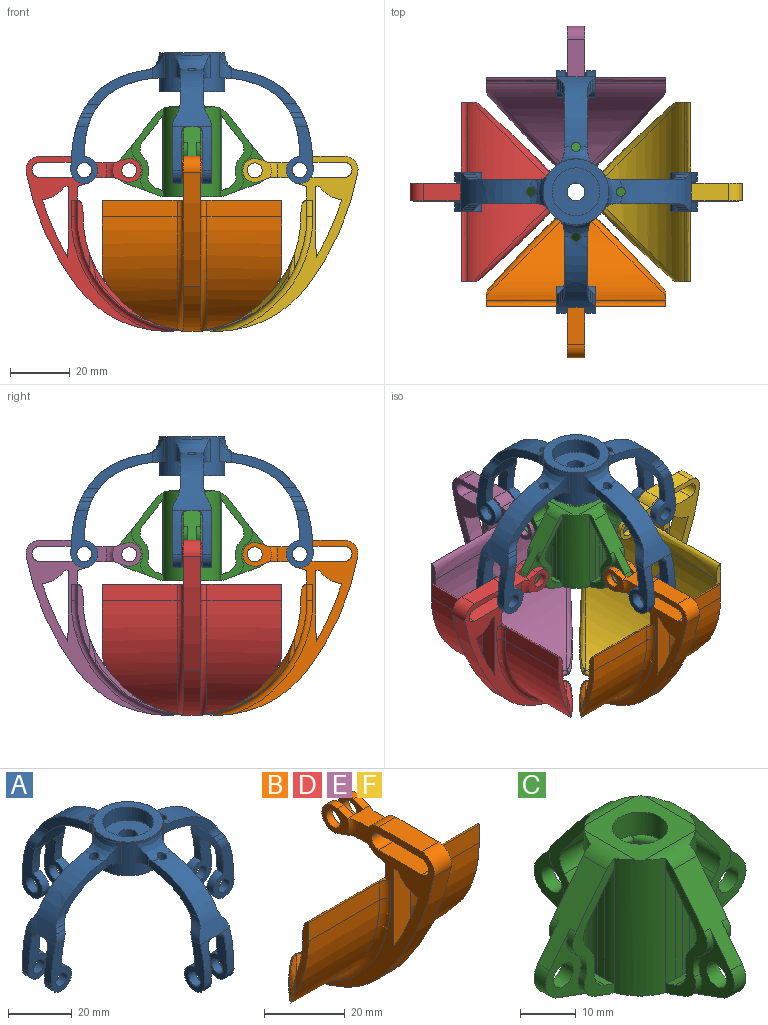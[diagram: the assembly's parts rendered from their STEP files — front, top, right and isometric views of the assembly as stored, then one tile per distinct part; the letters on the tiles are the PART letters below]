
ASSEMBLY  parts=6 mates=3
PART A: 124 faces, bbox 81x81x43.8 mm
  f0: extruded ~23.73x18.99mm, area 274.3mm2, adj f2,f27,f36,f37,f41,f42,f43,f44
  f1: extruded ~25.65x16.4mm, area 266.5mm2, adj f25,f33,f36,f37,f39,f42,f43,f44
  f2: bspline ~20.2x7.03mm, area 69.4mm2, adj f0,f33,f36,f37,f55,f56,f123
  f3: extruded ~23.73x18.99mm, area 274.3mm2, adj f5,f23,f57,f58,f62,f63,f64,f65
  f4: extruded ~25.65x16.4mm, area 266.5mm2, adj f21,f33,f57,f58,f60,f63,f64,f65
  f5: bspline ~20.2x7.03mm, area 63.5mm2, adj f3,f33,f57,f58,f76,f77,f122
  f6: extruded ~23.73x18.99mm, area 274.3mm2, adj f8,f19,f78,f79,f83,f84,f85,f86
  f7: extruded ~25.65x16.4mm, area 266.6mm2, adj f17,f33,f78,f79,f81,f84,f85,f86
  f8: bspline ~20.2x7.03mm, area 67.5mm2, adj f6,f33,f78,f79,f97,f98,f121
  f9: extruded ~23.73x18.99mm, area 274.3mm2, adj f11,f15,f99,f100,f104,f105,f106,f107
  f10: extruded ~25.65x16.4mm, area 266.5mm2, adj f13,f33,f99,f100,f102,f105,f106,f107
  f11: bspline ~20.2x7.03mm, area 63.5mm2, adj f9,f33,f99,f100,f118,f119,f120
  f12: cylinder r=4.5mm len=9mm, axis (-1,0,0), area 63.6mm2, adj f13,f15,f106,f114
  f13: extruded ~10x5mm, area 32.4mm2, adj f10,f12,f106,f114,f117
  f14: cylinder r=2.5mm len=5mm, axis (-1,0,0), area 47.1mm2, adj f106,f114
  f15: extruded ~14.5x5mm, area 46.1mm2, adj f9,f12,f106,f114,f117
  f16: cylinder r=4.5mm len=9mm, axis (0,-1,0), area 63.6mm2, adj f17,f19,f85,f93
  f17: extruded ~10x5mm, area 32.4mm2, adj f7,f16,f85,f93,f96
  f18: cylinder r=2.5mm len=5mm, axis (0,-1,0), area 47.1mm2, adj f85,f93
  f19: extruded ~14.5x5mm, area 46.1mm2, adj f6,f16,f85,f93,f96
  f20: cylinder r=4.5mm len=9mm, axis (1,0,0), area 63.6mm2, adj f21,f23,f64,f72
  f21: extruded ~10x5mm, area 32.4mm2, adj f4,f20,f64,f72,f75
  f22: cylinder r=2.5mm len=5mm, axis (1,0,0), area 47.1mm2, adj f64,f72
  f23: extruded ~14.5x5mm, area 46.1mm2, adj f3,f20,f64,f72,f75
  f24: cylinder r=4.5mm len=9mm, axis (0,1,0), area 63.6mm2, adj f25,f27,f43,f51
  f25: extruded ~10x5mm, area 32.4mm2, adj f1,f24,f43,f51,f54
  f26: cylinder r=2.5mm len=5mm, axis (0,1,0), area 47.1mm2, adj f43,f51
  f27: extruded ~14.5x5mm, area 46.1mm2, adj f0,f24,f43,f51,f54
  f28: cylinder r=3mm len=6mm, axis (0,0,-1), area 56.5mm2, adj f29,f30
  f29: plane 16x16mm, normal (0,0,1), area 172.8mm2, adj f28,f32
  f30: plane 16x16mm, normal (0,0,-1), area 172.8mm2, adj f28,f31
  f31: cylinder r=8mm len=16mm, axis (0,0,-1), area 251.3mm2, adj f30,f35
  f32: cylinder r=8mm len=16mm, axis (0,0,-1), area 251.3mm2, adj f29,f34
  f33: cylinder r=11mm len=22mm, axis (0,0,-1), area 490.5mm2, adj f1,f2,f4,f5,f7,f8,f10,f11
  f34: plane 22x22mm, normal (0,0,1), area 179.1mm2, adj f32,f33
  f35: plane 22x22mm, normal (0,0,-1), area 179.1mm2, adj f31,f33
  f36: plane 23.74x12.98mm, normal (0,-1,0), area 71mm2, adj f0,f1,f2,f49,f56
  f37: plane 23.68x12.9mm, normal (0,1,0), area 70.7mm2, adj f0,f1,f2,f47,f55
  f38: cylinder r=4.5mm len=9mm, axis (0,1,0), area 63.6mm2, adj f39,f41,f42,f52
  f39: extruded ~10x5mm, area 32.4mm2, adj f1,f38,f42,f52,f53
  f40: cylinder r=2.5mm len=5mm, axis (0,1,0), area 47.1mm2, adj f42,f52
  f41: extruded ~14.5x5mm, area 46.1mm2, adj f0,f38,f42,f52,f53
  f42: plane 19.26x9mm, normal (0,-1,0), area 88.8mm2, adj f0,f1,f38,f39,f40,f41,f48
  f43: plane 19.26x9mm, normal (0,1,0), area 89mm2, adj f0,f1,f24,f25,f26,f27,f46
  f44: plane 4.47x1.4mm, normal (0,-0.86,0.51), area 6.1mm2, adj f0,f1,f48,f49
  f45: plane 4.53x1.5mm, normal (0,0.86,0.5), area 6.6mm2, adj f0,f1,f46,f47
  f46: cylinder r=6mm len=4.91mm, axis (1,0,0), area 12.1mm2, adj f0,f1,f43,f45
  f47: cylinder r=6mm len=5.78mm, axis (1,0,0), area 12.5mm2, adj f0,f1,f37,f45
  f48: cylinder r=6mm len=4.92mm, axis (-1,0,0), area 12.3mm2, adj f0,f1,f42,f44
  f49: cylinder r=6mm len=5.77mm, axis (-1,0,0), area 12.6mm2, adj f0,f1,f36,f44
  f50: plane 3.83x3mm, normal (0,0,-1), area 11.5mm2, adj f0,f1,f53,f54
  f51: plane 17.19x9mm, normal (0,-1,0), area 80.9mm2, adj f24,f25,f26,f27,f54
  f52: plane 17.19x9mm, normal (0,1,0), area 80.9mm2, adj f38,f39,f40,f41,f53
  f53: cylinder r=2mm len=4.38mm, axis (1,0,0), area 12.1mm2, adj f39,f41,f50,f52
  f54: cylinder r=2mm len=4.38mm, axis (-1,0,0), area 12.1mm2, adj f25,f27,f50,f51
  f55: cylinder r=5mm len=8.04mm, axis (0,0,-1), area 27mm2, adj f1,f2,f33,f37
  f56: cylinder r=5mm len=8.04mm, axis (0,0,-1), area 27mm2, adj f1,f2,f33,f36
  f57: plane 23.74x12.98mm, normal (-1,0,0), area 71mm2, adj f3,f4,f5,f70,f77
  f58: plane 23.68x12.9mm, normal (1,0,0), area 70.7mm2, adj f3,f4,f5,f68,f76
  f59: cylinder r=4.5mm len=9mm, axis (1,0,0), area 63.6mm2, adj f60,f62,f63,f73
  f60: extruded ~10x5mm, area 32.4mm2, adj f4,f59,f63,f73,f74
  f61: cylinder r=2.5mm len=5mm, axis (1,0,0), area 47.1mm2, adj f63,f73
  f62: extruded ~14.5x5mm, area 46.1mm2, adj f3,f59,f63,f73,f74
  f63: plane 19.26x9mm, normal (-1,0,0), area 88.8mm2, adj f3,f4,f59,f60,f61,f62,f69
  f64: plane 19.26x9mm, normal (1,0,0), area 89mm2, adj f3,f4,f20,f21,f22,f23,f67
  f65: plane 4.47x1.4mm, normal (-0.86,0,0.51), area 6.1mm2, adj f3,f4,f69,f70
  f66: plane 4.53x1.5mm, normal (0.86,0,0.5), area 6.6mm2, adj f3,f4,f67,f68
  f67: cylinder r=6mm len=4.91mm, axis (0,-1,0), area 12.1mm2, adj f3,f4,f64,f66
  f68: cylinder r=6mm len=5.78mm, axis (0,-1,0), area 12.5mm2, adj f3,f4,f58,f66
  f69: cylinder r=6mm len=4.92mm, axis (0,1,0), area 12.3mm2, adj f3,f4,f63,f65
  f70: cylinder r=6mm len=5.77mm, axis (0,1,0), area 12.6mm2, adj f3,f4,f57,f65
  f71: plane 3.83x3mm, normal (0,0,-1), area 11.5mm2, adj f3,f4,f74,f75
  f72: plane 17.19x9mm, normal (-1,0,0), area 80.9mm2, adj f20,f21,f22,f23,f75
  f73: plane 17.19x9mm, normal (1,0,0), area 80.9mm2, adj f59,f60,f61,f62,f74
  f74: cylinder r=2mm len=4.38mm, axis (0,-1,0), area 12.1mm2, adj f60,f62,f71,f73
  f75: cylinder r=2mm len=4.38mm, axis (0,1,0), area 12.1mm2, adj f21,f23,f71,f72
  f76: cylinder r=5mm len=8.04mm, axis (0,0,-1), area 27mm2, adj f4,f5,f33,f58
  f77: cylinder r=5mm len=8.04mm, axis (0,0,-1), area 27mm2, adj f4,f5,f33,f57
  f78: plane 23.74x12.98mm, normal (0,1,0), area 71mm2, adj f6,f7,f8,f91,f98
  f79: plane 23.68x12.9mm, normal (0,-1,0), area 70.7mm2, adj f6,f7,f8,f89,f97
  f80: cylinder r=4.5mm len=9mm, axis (0,-1,0), area 63.6mm2, adj f81,f83,f84,f94
  f81: extruded ~10x5mm, area 32.4mm2, adj f7,f80,f84,f94,f95
  f82: cylinder r=2.5mm len=5mm, axis (0,-1,0), area 47.1mm2, adj f84,f94
  f83: extruded ~14.5x5mm, area 46.1mm2, adj f6,f80,f84,f94,f95
  f84: plane 19.26x9mm, normal (0,1,0), area 88.8mm2, adj f6,f7,f80,f81,f82,f83,f90
  f85: plane 19.26x9mm, normal (0,-1,0), area 89mm2, adj f6,f7,f16,f17,f18,f19,f88
  f86: plane 4.47x1.4mm, normal (0,0.86,0.51), area 6.1mm2, adj f6,f7,f90,f91
  f87: plane 4.53x1.5mm, normal (0,-0.86,0.5), area 6.6mm2, adj f6,f7,f88,f89
  f88: cylinder r=6mm len=4.91mm, axis (-1,0,0), area 12.1mm2, adj f6,f7,f85,f87
  f89: cylinder r=6mm len=5.78mm, axis (-1,0,0), area 12.5mm2, adj f6,f7,f79,f87
  f90: cylinder r=6mm len=4.92mm, axis (1,0,0), area 12.3mm2, adj f6,f7,f84,f86
  f91: cylinder r=6mm len=5.77mm, axis (1,0,0), area 12.6mm2, adj f6,f7,f78,f86
  f92: plane 3.83x3mm, normal (0,0,-1), area 11.5mm2, adj f6,f7,f95,f96
  f93: plane 17.19x9mm, normal (0,1,0), area 80.9mm2, adj f16,f17,f18,f19,f96
  f94: plane 17.19x9mm, normal (0,-1,0), area 80.9mm2, adj f80,f81,f82,f83,f95
  f95: cylinder r=2mm len=4.38mm, axis (-1,0,0), area 12.1mm2, adj f81,f83,f92,f94
  f96: cylinder r=2mm len=4.38mm, axis (1,0,0), area 12.1mm2, adj f17,f19,f92,f93
  f97: cylinder r=5mm len=8.04mm, axis (0,0,-1), area 27mm2, adj f7,f8,f33,f79
  f98: cylinder r=5mm len=8.04mm, axis (0,0,-1), area 27mm2, adj f7,f8,f33,f78
  f99: plane 23.74x12.98mm, normal (1,0,0), area 71mm2, adj f9,f10,f11,f112,f119
  f100: plane 23.68x12.9mm, normal (-1,0,0), area 70.7mm2, adj f9,f10,f11,f110,f118
  f101: cylinder r=4.5mm len=9mm, axis (-1,0,0), area 63.6mm2, adj f102,f104,f105,f115
  f102: extruded ~10x5mm, area 32.4mm2, adj f10,f101,f105,f115,f116
  f103: cylinder r=2.5mm len=5mm, axis (-1,0,0), area 47.1mm2, adj f105,f115
  f104: extruded ~14.5x5mm, area 46.1mm2, adj f9,f101,f105,f115,f116
  f105: plane 19.26x9mm, normal (1,0,0), area 88.8mm2, adj f9,f10,f101,f102,f103,f104,f111
  f106: plane 19.26x9mm, normal (-1,0,0), area 89mm2, adj f9,f10,f12,f13,f14,f15,f109
  f107: plane 4.47x1.4mm, normal (0.86,0,0.51), area 6.1mm2, adj f9,f10,f111,f112
  f108: plane 4.53x1.5mm, normal (-0.86,0,0.5), area 6.6mm2, adj f9,f10,f109,f110
  f109: cylinder r=6mm len=4.91mm, axis (0,1,0), area 12.1mm2, adj f9,f10,f106,f108
  f110: cylinder r=6mm len=5.78mm, axis (0,1,0), area 12.5mm2, adj f9,f10,f100,f108
  f111: cylinder r=6mm len=4.92mm, axis (0,-1,0), area 12.3mm2, adj f9,f10,f105,f107
  f112: cylinder r=6mm len=5.77mm, axis (0,-1,0), area 12.6mm2, adj f9,f10,f99,f107
  f113: plane 3.83x3mm, normal (0,0,-1), area 11.5mm2, adj f9,f10,f116,f117
  f114: plane 17.19x9mm, normal (1,0,0), area 80.9mm2, adj f12,f13,f14,f15,f117
  f115: plane 17.19x9mm, normal (-1,0,0), area 80.9mm2, adj f101,f102,f103,f104,f116
  f116: cylinder r=2mm len=4.38mm, axis (0,1,0), area 12.1mm2, adj f102,f104,f113,f115
  f117: cylinder r=2mm len=4.38mm, axis (0,-1,0), area 12.1mm2, adj f13,f15,f113,f114
  f118: cylinder r=5mm len=8.04mm, axis (0,0,-1), area 27mm2, adj f10,f11,f33,f100
  f119: cylinder r=5mm len=8.04mm, axis (0,0,-1), area 27mm2, adj f10,f11,f33,f99
  f120: cylinder r=1.5mm len=3.86mm, axis (0,0,1), area 29.6mm2, adj f9,f10,f11
  f121: cylinder r=1.5mm len=3.25mm, axis (0,0,1), area 30.2mm2, adj f6,f7,f8
  f122: cylinder r=1.5mm len=3.86mm, axis (0,0,1), area 29.6mm2, adj f3,f4,f5
  f123: cylinder r=1.5mm len=3.42mm, axis (0,0,1), area 28.1mm2, adj f0,f1,f2
PART B: 60 faces, bbox 65.3x62.2x65.6 mm
  f0: cylinder r=4mm len=8mm, axis (-1,0,0), area 34.4mm2, adj f1,f2,f3,f5
  f1: plane 3.56x2.25mm, normal (0,-0.34,-0.94), area 8.5mm2, adj f0,f3,f5,f31
  f2: plane 3.56x2.25mm, normal (0,-0.34,0.94), area 8.5mm2, adj f0,f3,f5,f32
  f3: plane 9.5x8mm, normal (1,0,0), area 40.4mm2, adj f0,f1,f2,f4,f59
  f4: cylinder r=2.5mm len=5mm, axis (-1,0,0), area 35.3mm2, adj f3,f5
  f5: plane 9.5x8mm, normal (-1,0,0), area 40.4mm2, adj f0,f1,f2,f4,f12
  f6: plane 3.56x2.25mm, normal (0,-0.34,0.94), area 8.5mm2, adj f8,f10,f11,f32
  f7: plane 3.56x2.25mm, normal (0,-0.34,-0.94), area 8.5mm2, adj f8,f10,f11,f31
  f8: cylinder r=4mm len=8mm, axis (-1,0,0), area 34.4mm2, adj f6,f7,f10,f11
  f9: cylinder r=2.5mm len=5mm, axis (-1,0,0), area 35.3mm2, adj f10,f11
  f10: plane 9.5x8mm, normal (-1,0,0), area 40.4mm2, adj f6,f7,f8,f9,f58
  f11: plane 9.5x8mm, normal (1,0,0), area 40.4mm2, adj f6,f7,f8,f9,f12
  f12: cylinder r=5.5mm len=5mm, axis (-1,0,0), area 18.2mm2, adj f5,f11,f31,f32
  f13: cylinder r=1.01mm len=2.01mm, axis (-1,0,0), area 1.1mm2, adj f14,f15,f50,f56
  f14: cylinder r=36.16mm len=60mm, axis (-1,0,0), area 2129.6mm2, adj f13,f17,f20,f24,f49,f50,f54,f56
  f15: cylinder r=38.11mm len=33.92mm, axis (-1,0,0), area 224.6mm2, adj f13,f18,f21,f36,f42,f43,f52,f57
  f16: cylinder r=38.16mm len=37.49mm, axis (-1,0,0), area 961.2mm2, adj f17,f18,f22,f47,f48,f52
  f17: plane 23.21x4.37mm, normal (-1,0,0), area 40.9mm2, adj f14,f16,f22,f24,f48,f49
  f18: torus R=40.16mm, axis (1,0,0), area 164.4mm2, adj f15,f16,f43,f44,f52
  f19: cylinder r=38.16mm len=37.49mm, axis (-1,0,0), area 961.2mm2, adj f20,f21,f23,f46,f53,f57
  f20: plane 23.21x4.92mm, normal (1,0,0), area 40.9mm2, adj f14,f19,f23,f24,f53,f54
  f21: torus R=40.16mm, axis (1,0,0), area 164.4mm2, adj f15,f19,f42,f45,f57
  f22: plane 25x5.49mm, normal (0,-1,0), area 137.2mm2, adj f16,f17,f24,f44
  f23: plane 25x5.49mm, normal (0,-1,0), area 137.2mm2, adj f19,f20,f24,f45
  f24: extruded ~60x5.49mm, area 384.5mm2, adj f14,f17,f20,f22,f23,f25,f42,f43
  f25: plane 6x4.56mm, normal (0,1,0), area 27.3mm2, adj f24,f29,f42,f43
  f26: cylinder r=2.5mm len=6mm, axis (-1,0,0), area 47.1mm2, adj f27,f41,f42,f43
  f27: plane 15x6mm, normal (0,0,1), area 90mm2, adj f26,f28,f42,f43
  f28: cylinder r=2.5mm len=6mm, axis (-1,0,0), area 47.1mm2, adj f27,f41,f42,f43
  f29: plane 6x3.69mm, normal (0,0.32,-0.95), area 23.3mm2, adj f25,f30,f42,f43
  f30: cylinder r=4.5mm len=6mm, axis (-1,0,0), area 17.8mm2, adj f29,f31,f42,f43
  f31: plane 8.09x6.45mm, normal (0,0,-1), area 39.7mm2, adj f1,f7,f12,f30,f42,f43,f58,f59
  f32: plane 8.09x6.45mm, normal (0,0,1), area 39.7mm2, adj f2,f6,f12,f33,f42,f43,f58,f59
  f33: cylinder r=4.5mm len=6mm, axis (-1,0,0), area 26.5mm2, adj f32,f34,f42,f43
  f34: plane 15x6mm, normal (0,0,1), area 90mm2, adj f33,f35,f42,f43
  f35: cylinder r=4.5mm len=6mm, axis (-1,0,0), area 47.6mm2, adj f34,f36,f42,f43
  f36: cylinder r=90.05mm len=37.99mm, axis (-1,0,0), area 252.4mm2, adj f15,f35,f42,f43
  f37: cylinder r=87.05mm len=19.2mm, axis (-1,0,0), area 126.9mm2, adj f38,f40,f42,f43
  f38: cylinder r=10.05mm len=7.42mm, axis (-1,0,0), area 53.9mm2, adj f37,f39,f42,f43
  f39: plane 6x1.32mm, normal (0,0,-1), area 7.9mm2, adj f38,f40,f42,f43
  f40: plane 23.7x6mm, normal (0,-1,0), area 142.2mm2, adj f37,f39,f42,f43
  f41: plane 15x6mm, normal (0,0,-1), area 90mm2, adj f26,f28,f42,f43
  f42: plane 57.67x41.36mm, normal (1,0,0), area 406.3mm2, adj f15,f21,f24,f25,f26,f27,f28,f29
  f43: plane 57.67x41.36mm, normal (-1,0,0), area 406.3mm2, adj f15,f18,f24,f25,f26,f27,f28,f29
  f44: cylinder r=2mm len=5.49mm, axis (0,0,1), area 17.2mm2, adj f18,f22,f24,f43
  f45: cylinder r=2mm len=5.49mm, axis (0,0,-1), area 17.2mm2, adj f21,f23,f24,f42
  f46: plane 12.95x11.89mm, normal (0.74,0.68,0), area 9.7mm2, adj f19,f53,f54,f57
  f47: plane 12.95x11.89mm, normal (-0.74,0.68,0), area 9.7mm2, adj f16,f48,f49,f52
  f48: cylinder r=3mm len=8.2mm, axis (0,0,-1), area 6.8mm2, adj f16,f17,f47,f49
  f49: bspline ~32.5x31.99mm, area 127.4mm2, adj f14,f17,f47,f48,f51
  f50: bspline ~10.2x3.61mm, area 0.2mm2, adj f13,f14,f51,f52
  f51: bspline ~25.81x19.01mm, area 22mm2, adj f49,f50,f52
  f52: bspline ~28.89x26.33mm, area 7.3mm2, adj f15,f16,f18,f47,f50,f51
  f53: cylinder r=3mm len=8.2mm, axis (0,0,1), area 6.8mm2, adj f19,f20,f46,f54
  f54: bspline ~32.5x31.99mm, area 127.4mm2, adj f14,f20,f46,f53,f55
  f55: bspline ~25.81x19.01mm, area 21.9mm2, adj f54,f56,f57
  f56: bspline ~10.2x3.61mm, area 0.2mm2, adj f13,f14,f55,f57
  f57: bspline ~28.89x26.33mm, area 7.3mm2, adj f15,f19,f21,f46,f55,f56
  f58: torus R=7.74mm, axis (1,0,0), area 13.1mm2, adj f10,f31,f32,f43
  f59: torus R=7.74mm, axis (1,0,0), area 13.1mm2, adj f3,f31,f32,f42
PART C: 117 faces, bbox 51.1x51.1x30.1 mm
  f0: cylinder r=10mm len=30mm, axis (0,0,-1), area 286.8mm2, adj f5,f6,f33,f41,f42,f44,f106,f113
  f1: cylinder r=10mm len=30mm, axis (0,0,-1), area 286.8mm2, adj f5,f6,f82,f89,f90,f91,f105,f113
  f2: cylinder r=10mm len=30mm, axis (0,0,-1), area 286.8mm2, adj f5,f6,f58,f65,f66,f67,f81,f89
  f3: cylinder r=5mm len=10mm, axis (0,0,-1), area 158.6mm2, adj f5,f15,f16,f17,f18,f19,f20
  f4: cylinder r=10mm len=30mm, axis (0,0,-1), area 286.8mm2, adj f5,f6,f34,f41,f42,f43,f57,f65
  f5: plane 15.15x15.15mm, normal (0,0,1), area 149mm2, adj f0,f1,f2,f3,f4,f42,f66,f90
  f6: plane 18.24x18.24mm, normal (0,0,-1), area 266.4mm2, adj f0,f1,f2,f4,f13,f41,f65,f89
  f7: plane 14x4.62mm, normal (0,-1,0), area 64.7mm2, adj f8,f12,f14,f17
  f8: plane 14x4mm, normal (-0.87,-0.5,0), area 64.7mm2, adj f7,f9,f14,f15
  f9: plane 14x4mm, normal (-0.87,0.5,0), area 64.7mm2, adj f8,f10,f14,f16
  f10: plane 14x4.62mm, normal (0,1,0), area 64.7mm2, adj f9,f11,f14,f18
  f11: plane 14x4mm, normal (0.87,0.5,0), area 64.7mm2, adj f10,f12,f14,f20
  f12: plane 14x4mm, normal (0.87,-0.5,0), area 64.7mm2, adj f7,f11,f14,f19
  f13: cylinder r=3mm len=10mm, axis (0,0,-1), area 188.5mm2, adj f6,f14
  f14: plane 9.24x8mm, normal (0,0,1), area 27.2mm2, adj f7,f8,f9,f10,f11,f12,f13
  f15: cylinder r=1mm len=4.83mm, axis (-0.5,0.87,0), area 6.6mm2, adj f3,f8,f16,f17
  f16: cylinder r=1mm len=4.83mm, axis (0.5,0.87,0), area 6.6mm2, adj f3,f9,f15,f18
  f17: cylinder r=1mm len=5mm, axis (-1,0,0), area 6.6mm2, adj f3,f7,f15,f19
  f18: cylinder r=1mm len=5mm, axis (1,0,0), area 6.6mm2, adj f3,f10,f16,f20
  f19: cylinder r=1mm len=4.83mm, axis (-0.5,-0.87,0), area 6.6mm2, adj f3,f12,f17,f20
  f20: cylinder r=1mm len=4.83mm, axis (0.5,-0.87,0), area 6.6mm2, adj f3,f11,f18,f19
  f21: plane 24.64x1.81mm, normal (-1,0,0), area 44.5mm2, adj f31,f32,f43,f44
  f22: cylinder r=4.5mm len=7.02mm, axis (0,1,0), area 25.5mm2, adj f24,f25,f27,f29
  f23: cylinder r=2.5mm len=5mm, axis (0,1,0), area 47.1mm2, adj f24,f25
  f24: plane 16.58x10.93mm, normal (0,-1,0), area 59.4mm2, adj f22,f23,f26,f27,f29,f37,f40
  f25: plane 16.58x10.93mm, normal (0,1,0), area 59.4mm2, adj f22,f23,f27,f28,f29,f35,f36
  f26: cylinder r=4.5mm len=5.48mm, axis (0,1,0), area 9.2mm2, adj f24,f33,f37,f40
  f27: plane 16.52x13.03mm, normal (-0.79,0,0.62), area 100.8mm2, adj f22,f24,f25,f33,f34,f35,f37,f42
  f28: cylinder r=4.5mm len=5.48mm, axis (0,1,0), area 9.2mm2, adj f25,f34,f35,f36
  f29: plane 11.71x6mm, normal (-0.34,0,-0.94), area 49.3mm2, adj f22,f24,f25,f33,f34,f36,f40,f41
  f30: cylinder r=6.5mm len=6mm, axis (0,1,0), area 37.6mm2, adj f33,f34,f38,f39
  f31: plane 8.86x6.99mm, normal (0.79,0,-0.62), area 64.2mm2, adj f21,f33,f34,f38,f43,f44
  f32: plane 6.08x2.63mm, normal (0.34,0,0.94), area 14mm2, adj f21,f33,f34,f39,f43,f44
  f33: plane 29.58x10.6mm, normal (0,-1,0), area 77.2mm2, adj f0,f26,f27,f29,f30,f31,f32,f37
  f34: plane 29.58x10.6mm, normal (0,1,0), area 77.2mm2, adj f4,f27,f28,f29,f30,f31,f32,f35
  f35: cylinder r=4mm len=5.76mm, axis (0,1,0), area 9.8mm2, adj f25,f27,f28,f34
  f36: cylinder r=4mm len=5.35mm, axis (0,1,0), area 9.8mm2, adj f25,f28,f29,f34
  f37: cylinder r=4mm len=5.76mm, axis (0,1,0), area 9.8mm2, adj f24,f26,f27,f33
  f38: cylinder r=4mm len=6mm, axis (0,1,0), area 34.3mm2, adj f30,f31,f33,f34
  f39: cylinder r=4mm len=6mm, axis (0,1,0), area 34.3mm2, adj f30,f32,f33,f34
  f40: cylinder r=4mm len=5.35mm, axis (0,1,0), area 9.8mm2, adj f24,f26,f29,f33
  f41: cylinder r=5mm len=8.21mm, axis (0,-1,0), area 10.9mm2, adj f0,f4,f6,f29,f33,f34
  f42: cylinder r=5mm len=13.05mm, axis (0,-1,0), area 35.2mm2, adj f0,f4,f5,f27,f33,f34
  f43: cylinder r=5mm len=25.39mm, axis (0,0,-1), area 53.9mm2, adj f4,f21,f31,f32
  f44: cylinder r=5mm len=25.39mm, axis (0,0,-1), area 53.9mm2, adj f0,f21,f31,f32
  f45: plane 24.64x1.81mm, normal (0,1,0), area 44.5mm2, adj f55,f56,f67,f68
  f46: cylinder r=4.5mm len=7.02mm, axis (1,0,0), area 25.5mm2, adj f48,f49,f51,f53
  f47: cylinder r=2.5mm len=5mm, axis (1,0,0), area 47.1mm2, adj f48,f49
  f48: plane 16.58x10.93mm, normal (-1,0,0), area 59.4mm2, adj f46,f47,f50,f51,f53,f61,f64
  f49: plane 16.58x10.93mm, normal (1,0,0), area 59.4mm2, adj f46,f47,f51,f52,f53,f59,f60
  f50: cylinder r=4.5mm len=5.48mm, axis (1,0,0), area 9.2mm2, adj f48,f57,f61,f64
  f51: plane 16.52x13.03mm, normal (0,0.79,0.62), area 100.8mm2, adj f46,f48,f49,f57,f58,f59,f61,f66
  f52: cylinder r=4.5mm len=5.48mm, axis (1,0,0), area 9.2mm2, adj f49,f58,f59,f60
  f53: plane 11.71x6mm, normal (0,0.34,-0.94), area 49.3mm2, adj f46,f48,f49,f57,f58,f60,f64,f65
  f54: cylinder r=6.5mm len=6mm, axis (1,0,0), area 37.6mm2, adj f57,f58,f62,f63
  f55: plane 8.86x6.99mm, normal (0,-0.79,-0.62), area 64.2mm2, adj f45,f57,f58,f62,f67,f68
  f56: plane 6.08x2.63mm, normal (0,-0.34,0.94), area 14mm2, adj f45,f57,f58,f63,f67,f68
  f57: plane 29.58x10.6mm, normal (-1,0,0), area 77.2mm2, adj f4,f50,f51,f53,f54,f55,f56,f61
  f58: plane 29.58x10.6mm, normal (1,0,0), area 77.2mm2, adj f2,f51,f52,f53,f54,f55,f56,f59
  f59: cylinder r=4mm len=5.76mm, axis (1,0,0), area 9.8mm2, adj f49,f51,f52,f58
  f60: cylinder r=4mm len=5.35mm, axis (1,0,0), area 9.8mm2, adj f49,f52,f53,f58
  f61: cylinder r=4mm len=5.76mm, axis (1,0,0), area 9.8mm2, adj f48,f50,f51,f57
  f62: cylinder r=4mm len=6mm, axis (1,0,0), area 34.3mm2, adj f54,f55,f57,f58
  f63: cylinder r=4mm len=6mm, axis (1,0,0), area 34.3mm2, adj f54,f56,f57,f58
  f64: cylinder r=4mm len=5.35mm, axis (1,0,0), area 9.8mm2, adj f48,f50,f53,f57
  f65: cylinder r=5mm len=8.21mm, axis (-1,0,0), area 10.9mm2, adj f2,f4,f6,f53,f57,f58
  f66: cylinder r=5mm len=13.05mm, axis (-1,0,0), area 35.2mm2, adj f2,f4,f5,f51,f57,f58
  f67: cylinder r=5mm len=25.39mm, axis (0,0,-1), area 53.9mm2, adj f2,f45,f55,f56
  f68: cylinder r=5mm len=25.39mm, axis (0,0,-1), area 53.9mm2, adj f4,f45,f55,f56
  f69: plane 24.64x1.81mm, normal (1,0,0), area 44.5mm2, adj f79,f80,f91,f92
  f70: cylinder r=4.5mm len=7.02mm, axis (0,-1,0), area 25.5mm2, adj f72,f73,f75,f77
  f71: cylinder r=2.5mm len=5mm, axis (0,-1,0), area 47.1mm2, adj f72,f73
  f72: plane 16.58x10.93mm, normal (0,1,0), area 59.4mm2, adj f70,f71,f74,f75,f77,f85,f88
  f73: plane 16.58x10.93mm, normal (0,-1,0), area 59.4mm2, adj f70,f71,f75,f76,f77,f83,f84
  f74: cylinder r=4.5mm len=5.48mm, axis (0,-1,0), area 9.2mm2, adj f72,f81,f85,f88
  f75: plane 16.52x13.03mm, normal (0.79,0,0.62), area 100.8mm2, adj f70,f72,f73,f81,f82,f83,f85,f90
  f76: cylinder r=4.5mm len=5.48mm, axis (0,-1,0), area 9.2mm2, adj f73,f82,f83,f84
  f77: plane 11.71x6mm, normal (0.34,0,-0.94), area 49.3mm2, adj f70,f72,f73,f81,f82,f84,f88,f89
  f78: cylinder r=6.5mm len=6mm, axis (0,-1,0), area 37.6mm2, adj f81,f82,f86,f87
  f79: plane 8.86x6.99mm, normal (-0.79,0,-0.62), area 64.2mm2, adj f69,f81,f82,f86,f91,f92
  f80: plane 6.08x2.63mm, normal (-0.34,0,0.94), area 14mm2, adj f69,f81,f82,f87,f91,f92
  f81: plane 29.58x10.6mm, normal (0,1,0), area 77.2mm2, adj f2,f74,f75,f77,f78,f79,f80,f85
  f82: plane 29.58x10.6mm, normal (0,-1,0), area 77.2mm2, adj f1,f75,f76,f77,f78,f79,f80,f83
  f83: cylinder r=4mm len=5.76mm, axis (0,-1,0), area 9.8mm2, adj f73,f75,f76,f82
  f84: cylinder r=4mm len=5.35mm, axis (0,-1,0), area 9.8mm2, adj f73,f76,f77,f82
  f85: cylinder r=4mm len=5.76mm, axis (0,-1,0), area 9.8mm2, adj f72,f74,f75,f81
  f86: cylinder r=4mm len=6mm, axis (0,-1,0), area 34.3mm2, adj f78,f79,f81,f82
  f87: cylinder r=4mm len=6mm, axis (0,-1,0), area 34.3mm2, adj f78,f80,f81,f82
  f88: cylinder r=4mm len=5.35mm, axis (0,-1,0), area 9.8mm2, adj f72,f74,f77,f81
  f89: cylinder r=5mm len=8.21mm, axis (0,1,0), area 10.9mm2, adj f1,f2,f6,f77,f81,f82
  f90: cylinder r=5mm len=13.05mm, axis (0,1,0), area 35.2mm2, adj f1,f2,f5,f75,f81,f82
  f91: cylinder r=5mm len=25.39mm, axis (0,0,-1), area 53.9mm2, adj f1,f69,f79,f80
  f92: cylinder r=5mm len=25.39mm, axis (0,0,-1), area 53.9mm2, adj f2,f69,f79,f80
  f93: plane 24.64x1.81mm, normal (0,-1,0), area 44.5mm2, adj f103,f104,f115,f116
  f94: cylinder r=4.5mm len=7.02mm, axis (-1,0,0), area 25.5mm2, adj f96,f97,f99,f101
  f95: cylinder r=2.5mm len=5mm, axis (-1,0,0), area 47.1mm2, adj f96,f97
  f96: plane 16.58x10.93mm, normal (1,0,0), area 59.4mm2, adj f94,f95,f98,f99,f101,f109,f112
  f97: plane 16.58x10.93mm, normal (-1,0,0), area 59.4mm2, adj f94,f95,f99,f100,f101,f107,f108
  f98: cylinder r=4.5mm len=5.48mm, axis (-1,0,0), area 9.2mm2, adj f96,f105,f109,f112
  f99: plane 16.52x13.03mm, normal (0,-0.79,0.62), area 100.8mm2, adj f94,f96,f97,f105,f106,f107,f109,f114
  f100: cylinder r=4.5mm len=5.48mm, axis (-1,0,0), area 9.2mm2, adj f97,f106,f107,f108
  f101: plane 11.71x6mm, normal (0,-0.34,-0.94), area 49.3mm2, adj f94,f96,f97,f105,f106,f108,f112,f113
  f102: cylinder r=6.5mm len=6mm, axis (-1,0,0), area 37.6mm2, adj f105,f106,f110,f111
  f103: plane 8.86x6.99mm, normal (0,0.79,-0.62), area 64.2mm2, adj f93,f105,f106,f110,f115,f116
  f104: plane 6.08x2.63mm, normal (0,0.34,0.94), area 14mm2, adj f93,f105,f106,f111,f115,f116
  f105: plane 29.58x10.6mm, normal (1,0,0), area 77.2mm2, adj f1,f98,f99,f101,f102,f103,f104,f109
  f106: plane 29.58x10.6mm, normal (-1,0,0), area 77.2mm2, adj f0,f99,f100,f101,f102,f103,f104,f107
  f107: cylinder r=4mm len=5.76mm, axis (-1,0,0), area 9.8mm2, adj f97,f99,f100,f106
  f108: cylinder r=4mm len=5.35mm, axis (-1,0,0), area 9.8mm2, adj f97,f100,f101,f106
  f109: cylinder r=4mm len=5.76mm, axis (-1,0,0), area 9.8mm2, adj f96,f98,f99,f105
  f110: cylinder r=4mm len=6mm, axis (-1,0,0), area 34.3mm2, adj f102,f103,f105,f106
  f111: cylinder r=4mm len=6mm, axis (-1,0,0), area 34.3mm2, adj f102,f104,f105,f106
  f112: cylinder r=4mm len=5.35mm, axis (-1,0,0), area 9.8mm2, adj f96,f98,f101,f105
  f113: cylinder r=5mm len=8.21mm, axis (1,0,0), area 10.9mm2, adj f0,f1,f6,f101,f105,f106
  f114: cylinder r=5mm len=13.05mm, axis (1,0,0), area 35.2mm2, adj f0,f1,f5,f99,f105,f106
  f115: cylinder r=5mm len=25.39mm, axis (0,0,-1), area 53.9mm2, adj f0,f93,f103,f104
  f116: cylinder r=5mm len=25.39mm, axis (0,0,-1), area 53.9mm2, adj f1,f93,f103,f104
PART D: same geometry as B
PART E: same geometry as B
PART F: same geometry as B
PLACE A t=(-0.11,-30.89,8.17)mm fixed
PLACE B rot(axis=(-1,0,0),0.4deg) t=(-0.11,-30.95,7.91)mm
PLACE C rot(axis=(1,0,0),0deg) t=(-0.11,-30.89,8.06)mm
PLACE D rot(axis=(0,0,-1),90deg) t=(-0.17,-30.89,7.91)mm
PLACE E rot(axis=(0,0,1),180deg) t=(-0.11,-30.83,7.91)mm
PLACE F rot(axis=(0,0,1),90deg) t=(-0.05,-30.89,7.91)mm
MATE slider C.f3 <-> A.f31  axis (0,0,1) through (-0.11,-30.89,38.06)mm
MATE revolute C.f94 <-> B.f0  axis (1,0,0) through (1.39,-51.89,16.85)mm
MATE pin_slot A.f12 <-> B.f28  axis (1,0,0) through (-3.61,-66.89,16.96)mm
